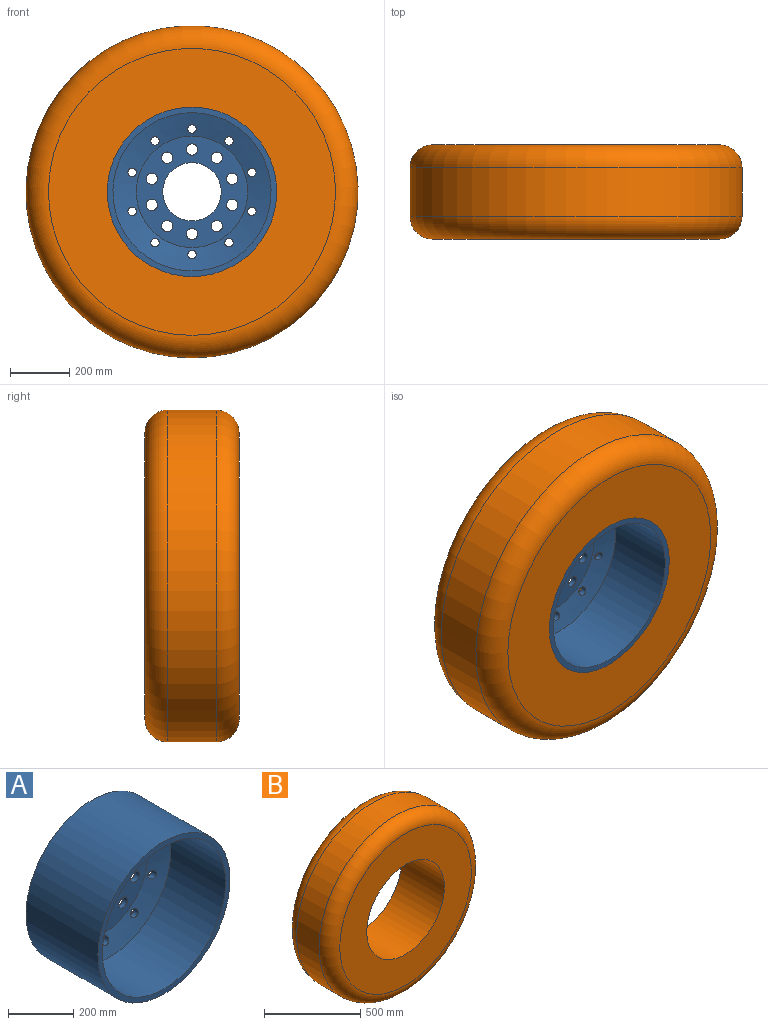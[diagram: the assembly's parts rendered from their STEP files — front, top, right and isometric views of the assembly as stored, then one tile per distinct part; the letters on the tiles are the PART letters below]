
ASSEMBLY  parts=2 mates=1
PART A: 34 faces, bbox 620.9x311.2x620.9 mm
  f0: cone r=190.5mm half-angle=73.3deg, axis (0,-1,0), area 85905.6mm2, adj f7,f8,f13,f14,f15,f16,f17,f18
  f1: cone r=185.03mm half-angle=73.3deg, axis (0,-1,0), area 111036.5mm2, adj f11,f12,f13,f14,f15,f16,f17,f18
  f2: cylinder r=285.75mm len=571.5mm, axis (0,1,0), area 558645mm2, adj f3,f4
  f3: plane 571.5x571.5mm, normal (0,-1,0), area 33062.7mm2, adj f2,f11
  f4: plane 571.5x571.5mm, normal (0,1,0), area 4540.1mm2, adj f2,f9
  f5: cylinder r=278.13mm len=556.26mm, axis (0,1,0), area 24413.2mm2, adj f6,f9
  f6: plane 556.26x556.26mm, normal (0,1,0), area 8796.4mm2, adj f5,f10
  f7: cylinder r=254mm len=508mm, axis (0,1,0), area 20268.3mm2, adj f0,f10
  f8: plane 381x381mm, normal (0,1,0), area 72174.1mm2, adj f0,f23,f24,f25,f26,f27,f28,f29
  f9: torus R=283.21mm, axis (0,-1,0), area 14037.3mm2, adj f4,f5
  f10: torus R=273.05mm, axis (0,1,0), area 49057.6mm2, adj f6,f7
  f11: cylinder r=266.7mm len=533.4mm, axis (0,1,0), area 396562.5mm2, adj f1,f3
  f12: plane 375.41x375.41mm, normal (0,-1,0), area 68852.1mm2, adj f1,f23,f24,f25,f26,f27,f28,f29
  f13: cylinder r=14.29mm len=28.58mm, axis (0,1,0), area 1785.4mm2, adj f0,f1
  f14: cylinder r=14.29mm len=28.58mm, axis (0,1,0), area 1785.5mm2, adj f0,f1
  f15: cylinder r=14.29mm len=28.58mm, axis (0,1,0), area 1785.4mm2, adj f0,f1
  f16: cylinder r=14.29mm len=28.58mm, axis (0,1,0), area 1785.5mm2, adj f0,f1
  f17: cylinder r=14.29mm len=28.58mm, axis (0,1,0), area 1785.5mm2, adj f0,f1
  f18: cylinder r=14.29mm len=28.58mm, axis (0,1,0), area 1785.4mm2, adj f0,f1
  f19: cylinder r=14.29mm len=28.58mm, axis (0,1,0), area 1785.4mm2, adj f0,f1
  f20: cylinder r=14.29mm len=28.58mm, axis (0,1,0), area 1785.5mm2, adj f0,f1
  f21: cylinder r=14.29mm len=28.58mm, axis (0,1,0), area 1785.3mm2, adj f0,f1
  f22: cylinder r=14.29mm len=28.58mm, axis (0,1,0), area 1785.4mm2, adj f0,f1
  f23: cylinder r=98.42mm len=196.85mm, axis (0,1,0), area 11780.9mm2, adj f8,f12
  f24: cylinder r=19.05mm len=38.1mm, axis (0,1,0), area 2280.2mm2, adj f8,f12
  f25: cylinder r=19.05mm len=38.1mm, axis (0,1,0), area 2280.2mm2, adj f8,f12
  f26: cylinder r=19.05mm len=38.1mm, axis (0,1,0), area 2280.2mm2, adj f8,f12
  f27: cylinder r=19.05mm len=38.1mm, axis (0,1,0), area 2280.2mm2, adj f8,f12
  f28: cylinder r=19.05mm len=38.1mm, axis (0,1,0), area 2280.2mm2, adj f8,f12
  f29: cylinder r=19.05mm len=38.1mm, axis (0,1,0), area 2280.2mm2, adj f8,f12
  f30: cylinder r=19.05mm len=38.1mm, axis (0,1,0), area 2280.2mm2, adj f8,f12
  f31: cylinder r=19.05mm len=38.1mm, axis (0,1,0), area 2280.2mm2, adj f8,f12
  f32: cylinder r=19.05mm len=38.1mm, axis (0,1,0), area 2280.2mm2, adj f8,f12
  f33: cylinder r=19.05mm len=38.1mm, axis (0,1,0), area 2280.2mm2, adj f8,f12
PART B: 6 faces, bbox 1212.4x317.5x1212.4 mm
  f0: cylinder r=285.75mm len=571.5mm, axis (0,1,0), area 570045.9mm2, adj f2,f3
  f1: cylinder r=560.07mm len=1120.14mm, axis (0,1,0), area 580990.8mm2, adj f4,f5
  f2: plane 967.74x967.74mm, normal (0,-1,0), area 479021mm2, adj f0,f5
  f3: plane 967.74x967.74mm, normal (0,1,0), area 479021mm2, adj f0,f4
  f4: torus R=483.87mm, axis (0,-1,0), area 400384.1mm2, adj f1,f3
  f5: torus R=483.87mm, axis (0,-1,0), area 400384.1mm2, adj f1,f2
PLACE A t=(-153.67,53.74,-19.68)mm
PLACE B t=(-153.67,-98.66,-19.68)mm
MATE fastened B.f0 <-> A.f2  axis (0,1,0) through (-153.67,-257.41,-19.68)mm
